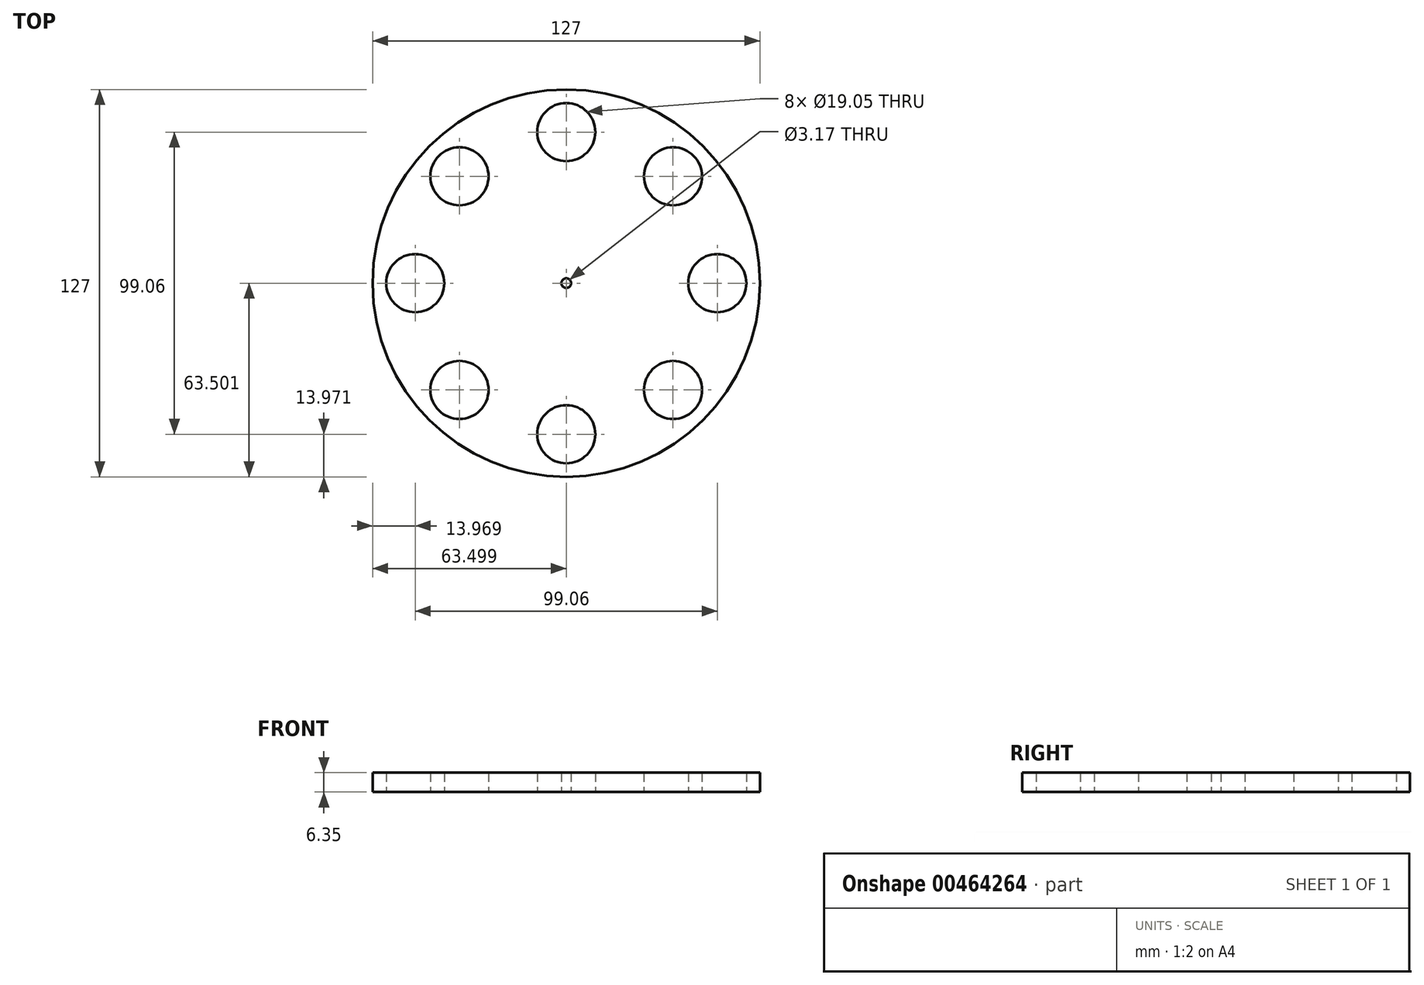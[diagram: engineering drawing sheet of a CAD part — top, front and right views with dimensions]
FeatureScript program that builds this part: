
annotation { "Feature Type Name" : "Feature", "Feature Type Description" : "" }
export const myFeature = defineFeature(function(context is Context, id is Id, definition is map)
    precondition{}
    {
        {
            var Q0;
            Q0=qCreatedBy(makeId("Top.planeOp"),FACE);
            var sketch = newSketch(context, id + "F0", { "sketchPlane" : qUnion([Q0])});
            skCircle(sketch, "E0", {"center": v(-1.98, 4.96) * mm, "radius": 63.5 * mm});
            skCircle(sketch, "E1", {"center": v(-1.98, 4.96) * mm, "radius": 34.93 * mm});
            skCircle(sketch, "E2", {"center": v(-37, 39.98) * mm, "radius": 9.53 * mm});
            skCircle(sketch, "E3", {"center": v(-1.98, 54.5) * mm, "radius": 9.53 * mm});
            skCircle(sketch, "E4", {"center": v(33.04, 39.98) * mm, "radius": 9.53 * mm});
            skCircle(sketch, "E5", {"center": v(47.55, 4.96) * mm, "radius": 9.53 * mm});
            skCircle(sketch, "E6", {"center": v(33.04, -30.06) * mm, "radius": 9.53 * mm});
            skCircle(sketch, "E7", {"center": v(-1.98, -44.57) * mm, "radius": 9.53 * mm});
            skCircle(sketch, "E8", {"center": v(-37, -30.06) * mm, "radius": 9.53 * mm});
            skCircle(sketch, "E9", {"center": v(-51.51, 4.96) * mm, "radius": 9.53 * mm});
            skCircle(sketch, "E10", {"center": v(-1.98, 4.96) * mm, "radius": 1.59 * mm});
            skSolve(sketch);
        }
        {
            var Q0;
            Q0=makeQuery(id+"F0.imprint","IMPRINT",FACE,{"disambiguationData":[TD([[makeQuery(id+"F0.imprint","IMPRINT",EDGE,{"derivedFrom":sQuery(id+"F0.wireOp",EDGE,"E0")}),1.0]])]});
            var Q1;
            Q1=makeQuery(id+"F0.imprint","IMPRINT",FACE,{"disambiguationData":[TD([[makeQuery(id+"F0.imprint","IMPRINT",EDGE,{"derivedFrom":sQuery(id+"F0.wireOp",EDGE,"E1")}),1.0]])]});
            extrude(context, id + "F1", {"entities" : qUnion([Q0, Q1]), "depth" : 6.35 * mm, "offsetDistance" : 25.4 * mm});
        }
    });
